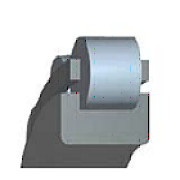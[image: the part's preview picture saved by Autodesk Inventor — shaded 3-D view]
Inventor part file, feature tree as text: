
AUTODESK INVENTOR PART (.ipt)
format: ipt  version: 2022 (Build 260153000, 153)  size: 163,840 bytes
history: native  units: mm (DEFAULTED — no unit token found)
features: other x1, sketch x1
ambient origin geometry x8: Origin, YZ Plane, XZ Plane, XY Plane, X Axis, Y Axis, Z Axis, Center Point
bodies: Solid1 (feature_tree)
feature tree (2):
  other  "轴承体"
  sketch  "草图"  dims[d0=6.0mm d1=9.0mm d2=12.666667mm d3=20.0mm d4=90.0deg d5=0.275mm d6=0.0mm d7=0.0mm d8=0.0mm d9=0.0mm d10=0.0mm]
